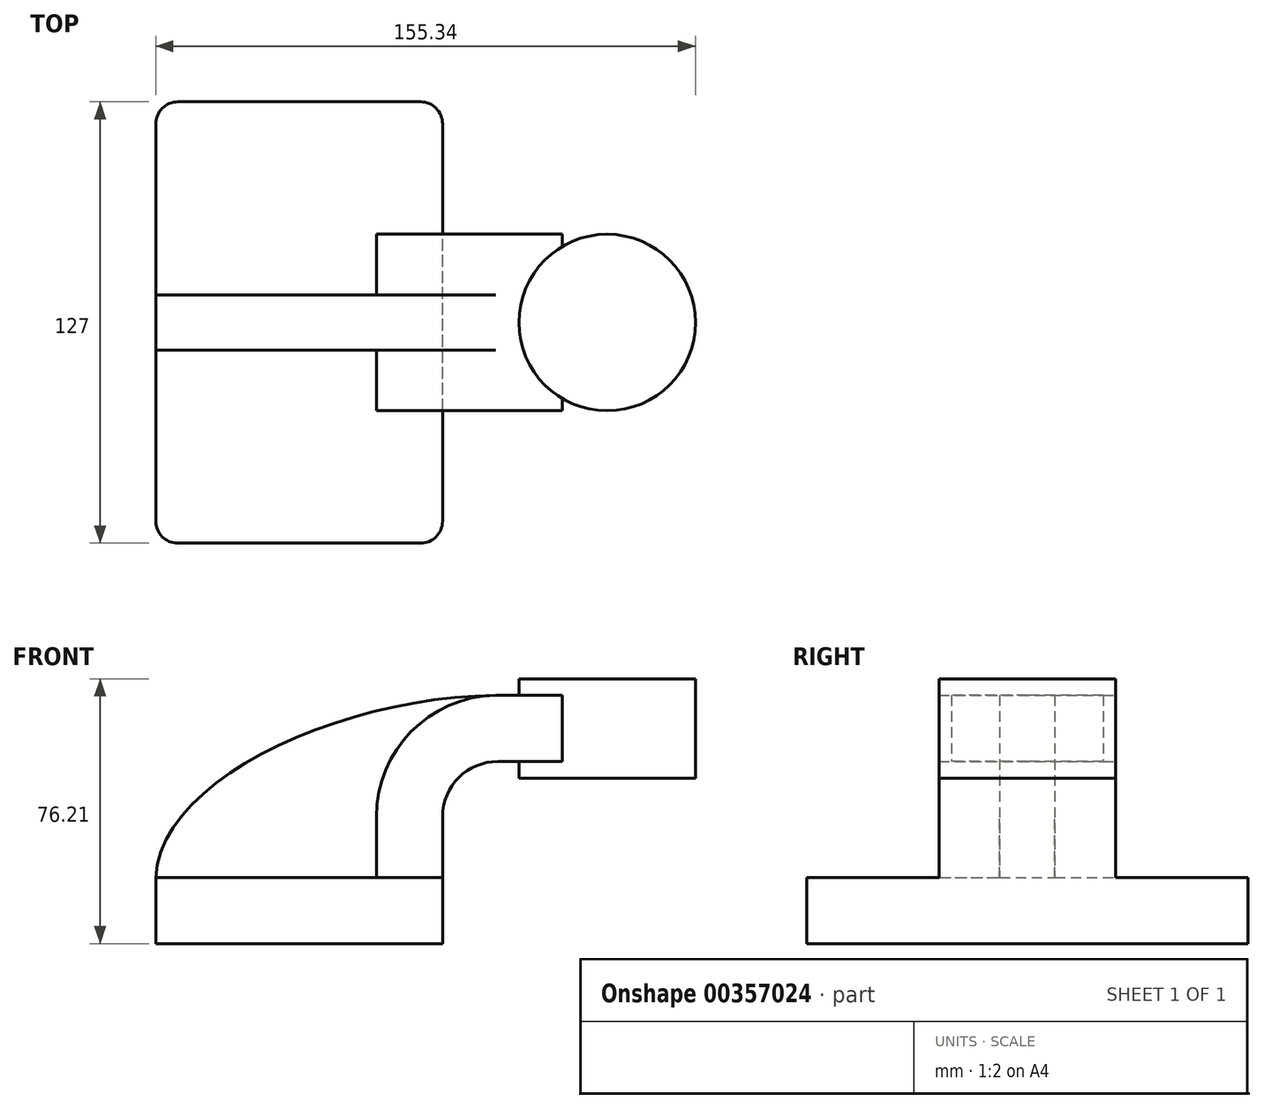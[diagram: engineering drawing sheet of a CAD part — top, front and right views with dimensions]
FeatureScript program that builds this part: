
annotation { "Feature Type Name" : "Feature", "Feature Type Description" : "" }
export const myFeature = defineFeature(function(context is Context, id is Id, definition is map)
    precondition{}
    {
        {
            var Q0;
            Q0=qCreatedBy(makeId("Front.planeOp"),FACE);
            var sketch = newSketch(context, id + "F0", { "sketchPlane" : qUnion([Q0])});
            skLineSegment(sketch, "E0.bottom", {"start": v(-41.28, 9.52) * mm, "end": v(41.27, 9.53) * mm});
            skLineSegment(sketch, "E0.top", {"start": v(-41.28, -9.53) * mm, "end": v(41.28, -9.53) * mm});
            skLineSegment(sketch, "E0.left", {"start": v(-41.28, 9.52) * mm, "end": v(-41.28, -9.53) * mm});
            skLineSegment(sketch, "E0.right", {"start": v(41.27, 9.53) * mm, "end": v(41.28, -9.52) * mm});
            skPoint(sketch, "E0.middle", {"position": v(0, 0) * mm});
            skLineSegment(sketch, "E1.bottom", {"start": v(114.06, 38.1) * mm, "end": v(63.26, 38.1) * mm});
            skLineSegment(sketch, "E1.top", {"start": v(114.06, 66.68) * mm, "end": v(63.26, 66.68) * mm});
            skLineSegment(sketch, "E1.left", {"start": v(114.06, 38.1) * mm, "end": v(114.06, 66.68) * mm});
            skLineSegment(sketch, "E1.right", {"start": v(63.26, 38.1) * mm, "end": v(63.26, 66.68) * mm});
            skPoint(sketch, "E1.middle", {"position": v(88.66, 52.39) * mm});
            skLineSegment(sketch, "E2", {"start": v(41.27, 9.53) * mm, "end": v(41.27, 27) * mm});
            skArc(sketch, "E3", {"start": v(41.27, 27) * mm, "mid": v(45.92, 38.23) * mm, "end": v(57.15, 42.88) * mm});
            skLineSegment(sketch, "E4", {"start": v(57.15, 42.88) * mm, "end": v(75.68, 42.88) * mm});
            skLineSegment(sketch, "E5.0", {"start": v(57.15, 61.93) * mm, "end": v(75.68, 61.93) * mm});
            skArc(sketch, "E5.1", {"start": v(22.22, 27) * mm, "mid": v(32.45, 51.7) * mm, "end": v(57.15, 61.93) * mm});
            skLineSegment(sketch, "E5.2", {"start": v(22.22, 9.53) * mm, "end": v(22.22, 27) * mm});
            skFitSpline(sketch, "E6", {"points": [v(57.15, 61.93) * mm, v(-41.28, 9.52) * mm], "startDerivative": vector(-133.52, -0.9) * mm, "endDerivative": vector(-4.14, -86.04) * mm});
            skLineSegment(sketch, "E7", {"start": v(75.68, 61.93) * mm, "end": v(75.68, 42.88) * mm});
            skLineSegment(sketch, "E8", {"start": v(88.66, 38.1) * mm, "end": v(88.66, 66.68) * mm});
            skSolve(sketch);
        }
        {
            var Q0;
            Q0=makeQuery(id+"F0.imprint","IMPRINT",FACE,{"disambiguationData":[TD([[makeQuery(id+"F0.imprint","IMPRINT",EDGE,{"derivedFrom":sQuery(id+"F0.wireOp",EDGE,"E0.top")}),1.0]])]});
            extrude(context, id + "F1", {"entities" : qUnion([Q0]), "endBound" : BoundingType.SYMMETRIC, "depth" : 127 * mm});
        }
        {
            var Q0;
            Q0=makeQuery(id+"F1.opExtrude","CAP_EDGE",EDGE,{"disambiguationData":[OSD([sQuery(id+"F0.wireOp",EDGE,"E0.right")])],"isStart":false});
            var Q1;
            Q1=makeQuery(id+"F1.opExtrude","CAP_EDGE",EDGE,{"disambiguationData":[OSD([sQuery(id+"F0.wireOp",EDGE,"E0.left")])],"isStart":false});
            var Q2;
            Q2=makeQuery(id+"F1.opExtrude","CAP_EDGE",EDGE,{"disambiguationData":[OSD([sQuery(id+"F0.wireOp",EDGE,"E0.left")])],"isStart":true});
            var Q3;
            Q3=makeQuery(id+"F1.opExtrude","CAP_EDGE",EDGE,{"disambiguationData":[OSD([sQuery(id+"F0.wireOp",EDGE,"E0.right")])],"isStart":true});
            fillet(context, id + "F2", {"entities" : qUnion([Q0, Q1, Q2, Q3]), "radius" : 6.35 * mm, "tangentPropagation" : true, "allowEdgeOverflow" : false});
        }
        {
            var Q0;
            {var subQ0=sQuery(id+"F0.wireOp",EDGE,"E1.left");Q0=makeQuery(id+"F0.imprint","IMPRINT",FACE,{"disambiguationData":[TD([[makeQuery(id+"F0.imprint","IMPRINT",EDGE,{"derivedFrom":subQ0}),1.0]])]});}
            var Q1;
            Q1=sQuery(id+"F0.wireOp",EDGE,"E8");
            revolve(context, id + "F3", {"operationType" : NewBodyOperationType.ADD, "entities" : qUnion([Q0]), "axis" : qUnion([Q1]), "revolveType" : RevolveType.FULL});
        }
        {
            var Q0;
            {var subQ3=sQuery(id+"F0.wireOp",EDGE,"E5.2");Q0=makeQuery(id+"F0.imprint","IMPRINT",FACE,{"disambiguationData":[TD([[makeQuery(id+"F0.imprint","IMPRINT",EDGE,{"derivedFrom":subQ3}),1.0]])]});}
            extrude(context, id + "F4", {"entities" : qUnion([Q0]), "operationType" : NewBodyOperationType.ADD, "endBound" : BoundingType.SYMMETRIC, "depth" : 15.88 * mm});
        }
        {
            var Q0;
            {var subQ1=sQuery(id+"F0.wireOp",EDGE,"E2");Q0=makeQuery(id+"F0.imprint","IMPRINT",FACE,{"disambiguationData":[TD([[makeQuery(id+"F0.imprint","IMPRINT",EDGE,{"derivedFrom":subQ1}),1.0]])]});}
            var Q1;
            {var subQ5=sQuery(id+"F0.wireOp",EDGE,"E7");Q1=makeQuery(id+"F0.imprint","IMPRINT",FACE,{"disambiguationData":[TD([[makeQuery(id+"F0.imprint","IMPRINT",EDGE,{"derivedFrom":subQ5}),-1.0]])]});}
            extrude(context, id + "F5", {"entities" : qUnion([Q0, Q1]), "operationType" : NewBodyOperationType.ADD, "endBound" : BoundingType.SYMMETRIC, "depth" : 50.8 * mm});
        }
    });
